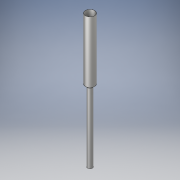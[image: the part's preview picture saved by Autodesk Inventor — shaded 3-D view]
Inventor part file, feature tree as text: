
AUTODESK INVENTOR PART (.ipt)
format: ipt  version: 2018 (Build 220112000, 112)  size: 127,488 bytes
history: native  units: in
note: dims shown in document units (in); Inventor stores cm internally (conversion verified against a paired STEP export)
features: extrude x4, sketch x4, fillet x2
ambient origin geometry x8: Origin, YZ Plane, XZ Plane, XY Plane, X Axis, Y Axis, Z Axis, Center Point
bodies: Solid1 (feature_tree)
feature tree (10):
  extrude  "Extrusion1"  Depth=0.037in
  extrude  "Extrusion2"  Depth=13.0906in
  extrude  "Extrusion3"  Depth=0.037in
  extrude  "Extrusion4"  Depth=0.037in
  fillet  "Fillet1"  Radius=15.0in
  fillet  "Fillet2"  Radius=0.125in
  sketch  "Sketch1"  dims[d0=2.005in d1=0.037in]
  sketch  "Sketch2"  dims[d2=13.0906in d3=0.0in d4=1.125in]
  sketch  "Sketch3"  dims[d5=0.037in d6=0.0in d7=0.037in]
  sketch  "Sketch4"  dims[d8=0.465in d9=0.0in d10=0.037in d11=15.0in d12=0.2in d13=0.0in d14=0.0in d15=0.125in d16=0.02in]
